# Revit family: RN 91002 Optifitt-Serra-Té
name_source: partatom
category: Rohrformteile
units: mm (PartAtom-declared; Revit-internal decimal feet)

## family parameters
Arbeitsebenenbasiert = Nein
Beim Laden mit Abzugskörper schneiden = Nein
Bemaßung runder Anschluss = Durchmesser verwenden
Gemeinsam genutzt = Nein
Immer vertikal = Ja
Teiletyp = T-Stück

## types (3) — shared parameters
1.010.00.2 Blattnummer der Richtlinie = 29
1.010.00.3 Ausgabedatum (Monat) der Richtlinie = 201308
1.010.00.4 Herstellername = R. Nussbaum AG
1.010.00.5 Revisionsdatum der Datei = 20190521
1.010.00.6 Webadresse des Herstellers = http://www.nussbaum.ch
1.100.00.4 Produktbezeichnung = Versorgung
1.110.00.2 Index = 3
1.110.00.4 Produktbezeichnung = Optifitt-Serra
1.960/3L.00.8 Link (URL) = https://www.nussbaum.ch
29.700.00.4 Produktname = Optifitt-Serra-T-Stück
29.700.00.5 Produktkennung = 2
29.700.00.6 Querschnittsform = 1
29.700.00.7 Nennweitensystem = DN
29.700.00.8 Nenndrucksystem = PN
29.710.02.4 Nenndruck = 16
29.710.02.5 max. zul. Überdruck [hPa] = 1600
29.710.02.7 max. zul. Dauer-Betriebsdruck [hPa] = 1600
29.710.02.9 max. zul. Dauer-Betriebstemperatur [°C] = 90
Connector Visibility = Nein
EnclosingSpace Visibility = Nein
Hersteller = R. Nussbaum AG
URL = https://www.nussbaum.ch

## per-type parameters (varying)
- DN=20: 1.800.00.3 TGA-Nummer=01900300000000000000000000000000000000000000000007000000000000000018; 1.800.00.4 Kommentarfeld=91002.55, Optifitt-Serra-T-Stück, DN=20, L=34, Rp=¾; 1.810.00.3 Hersteller-Bestellnummer=91002.55; 1.810.00.4 DATANORM-Nummer=91002.55; 1.810.00.5 StLB-Nummer=213.113; 1.810.00.6 GTIN-Nummer=7612945035738; 29.710.02.10 Formstück-Gewicht [kg]=0.001; 29.710.02.3 Benennung=Optifitt-Serra-T-Stück, DN=20, L=34, Rp=¾; CONNECTOR0_DIAMETER_dX_0r=20 mm; CONNECTOR0_dX_00=34 mm; CONNECTOR0_dX_01=19 mm  [stored 0.062336 ft]; CONNECTOR0_ref_dX=19 mm  [stored 0.062336 ft]; CONNECTOR1_DIAMETER_dX_0r=20 mm; CONNECTOR1_dX_00=19 mm  [stored 0.062336 ft]; CONNECTOR1_dX_01=34 mm; CONNECTOR1_ref_dX=19 mm  [stored 0.062336 ft]; CONNECTOR2_DIAMETER_dY_0r=20 mm; CONNECTOR2_dY_00=34 mm; CONNECTOR2_dY_01=19 mm  [stored 0.062336 ft]; CONNECTOR2_ref_dY=19 mm  [stored 0.062336 ft]; Modell=91002.55; R. Nussbaum AG 91002.53 de Visibility=Nein; R. Nussbaum AG 91002.54 de Visibility=Nein; R. Nussbaum AG 91002.55 de Visibility=Ja; Typenkommentare=Optifitt-Serra-Té  DN=20
- DN=15: 1.800.00.3 TGA-Nummer=01900300000000000000000000000000000000000000000007000000000000000017; 1.800.00.4 Kommentarfeld=91002.54, Optifitt-Serra-T-Stück, DN=15, L=30, Rp=½; 1.810.00.3 Hersteller-Bestellnummer=91002.54; 1.810.00.4 DATANORM-Nummer=91002.54; 1.810.00.5 StLB-Nummer=213.112; 1.810.00.6 GTIN-Nummer=7612945035721; 29.710.02.10 Formstück-Gewicht [kg]=0.096; 29.710.02.3 Benennung=Optifitt-Serra-T-Stück, DN=15, L=30, Rp=½; CONNECTOR0_DIAMETER_dX_0r=15 mm; CONNECTOR0_dX_00=30 mm; CONNECTOR0_dX_01=17 mm; CONNECTOR0_ref_dX=17 mm; CONNECTOR1_DIAMETER_dX_0r=15 mm; CONNECTOR1_dX_00=17 mm; CONNECTOR1_dX_01=30 mm; CONNECTOR1_ref_dX=17 mm; CONNECTOR2_DIAMETER_dY_0r=15 mm; CONNECTOR2_dY_00=30 mm; CONNECTOR2_dY_01=17 mm; CONNECTOR2_ref_dY=17 mm; Modell=91002.54; R. Nussbaum AG 91002.53 de Visibility=Nein; R. Nussbaum AG 91002.54 de Visibility=Ja; R. Nussbaum AG 91002.55 de Visibility=Nein; Typenkommentare=Optifitt-Serra-Té  DN=15
- DN=10: 1.800.00.3 TGA-Nummer=01900300000000000000000000000000000000000000000007000000000000000016; 1.800.00.4 Kommentarfeld=91002.53, Optifitt-Serra-T-Stück, DN=10, L=22, Rp=3/8; 1.810.00.3 Hersteller-Bestellnummer=91002.53; 1.810.00.4 DATANORM-Nummer=91002.53; 1.810.00.5 StLB-Nummer=213.111; 1.810.00.6 GTIN-Nummer=7612945035714; 29.710.02.10 Formstück-Gewicht [kg]=0.063; 29.710.02.3 Benennung=Optifitt-Serra-T-Stück, DN=10, L=22, Rp=3/8; CONNECTOR0_DIAMETER_dX_0r=10 mm  [stored 0.0328084 ft]; CONNECTOR0_dX_00=22 mm; CONNECTOR0_dX_01=12 mm  [stored 0.0393701 ft]; CONNECTOR0_ref_dX=12 mm  [stored 0.0393701 ft]; CONNECTOR1_DIAMETER_dX_0r=10 mm  [stored 0.0328084 ft]; CONNECTOR1_dX_00=12 mm  [stored 0.0393701 ft]; CONNECTOR1_dX_01=22 mm; CONNECTOR1_ref_dX=12 mm  [stored 0.0393701 ft]; CONNECTOR2_DIAMETER_dY_0r=10 mm  [stored 0.0328084 ft]; CONNECTOR2_dY_00=22 mm; CONNECTOR2_dY_01=12 mm  [stored 0.0393701 ft]; CONNECTOR2_ref_dY=12 mm  [stored 0.0393701 ft]; Modell=91002.53; R. Nussbaum AG 91002.53 de Visibility=Ja; R. Nussbaum AG 91002.54 de Visibility=Nein; R. Nussbaum AG 91002.55 de Visibility=Nein; Typenkommentare=Optifitt-Serra-Té  DN=10

note: [stored X ft] marks values corroborated as IEEE doubles in the binary element streams (Revit-internal decimal feet)

## geometry (parser evidence)
native form markers: Sweep x2
no freeform markers — native parametric forms only
